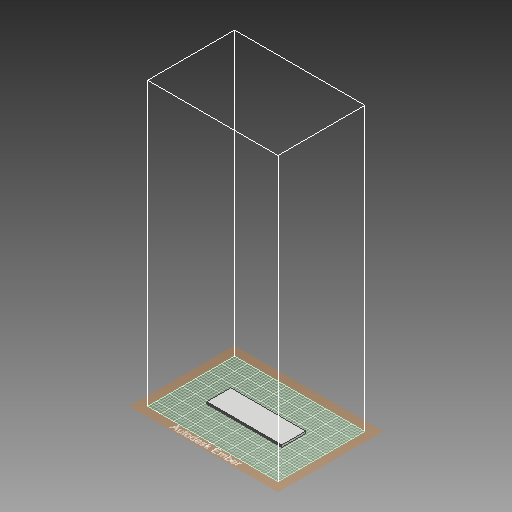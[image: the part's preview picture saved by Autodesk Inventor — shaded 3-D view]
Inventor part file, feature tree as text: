
AUTODESK INVENTOR PART (.ipt)
format: ipt  version: 2018.3 (Build 223284000, 284)  size: 237,056 bytes
history: native  units: mm
features: extrude x3, sketch x3
ambient origin geometry x8: Origin, YZ Plane, XZ Plane, XY Plane, X Axis, Y Axis, Z Axis, Center Point
bodies: Solid1 (feature_tree)
feature tree (6):
  extrude  "Extrusion1"  Depth=20.0mm
  extrude  "Extrusion2"  Depth=0.5mm
  extrude  "Extrusion3"  Depth=0.4mm
  sketch  "Sketch1"  dims[d0=34.5mm d1=20.0mm]
  sketch  "Sketch2"  dims[d2=1.0mm d3=0.0mm d4=0.5mm]
  sketch  "Sketch3"  dims[d5=0.3mm d6=0.4mm d7=0.15mm d8=34.5mm d9=0.0mm d10=0.1mm d11=0.15mm d12=0.0mm]
